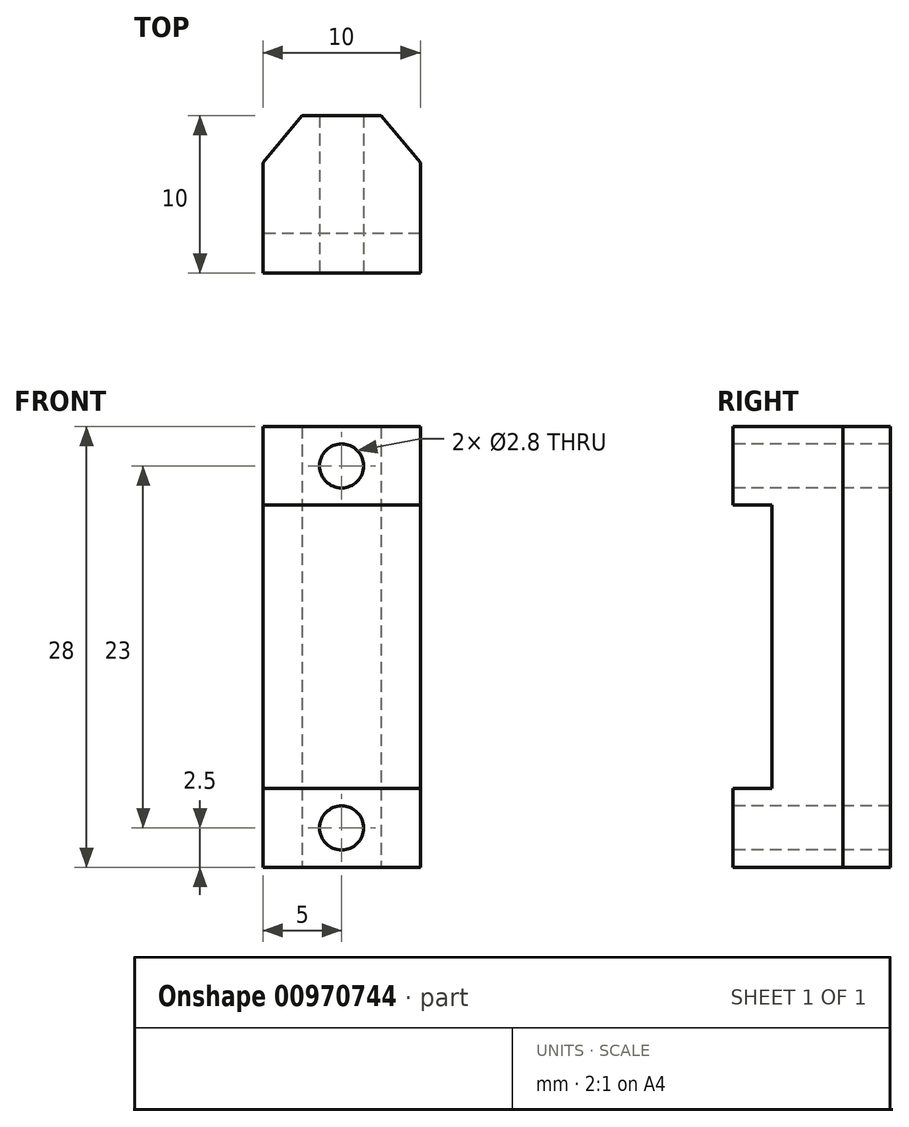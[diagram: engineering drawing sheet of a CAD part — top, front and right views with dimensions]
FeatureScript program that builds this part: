
annotation { "Feature Type Name" : "Feature", "Feature Type Description" : "" }
export const myFeature = defineFeature(function(context is Context, id is Id, definition is map)
    precondition{}
    {
        {
            var Q0;
            Q0=qCreatedBy(makeId("Top.planeOp"),FACE);
            var sketch = newSketch(context, id + "F0", { "sketchPlane" : qUnion([Q0])});
            skLineSegment(sketch, "E0.bottom", {"start": v(0, 0) * mm, "end": v(10, 0) * mm});
            skLineSegment(sketch, "E0.top", {"start": v(2.5, 10) * mm, "end": v(7.5, 10) * mm});
            skLineSegment(sketch, "E0.left", {"start": v(0, 0) * mm, "end": v(0, 7) * mm});
            skLineSegment(sketch, "E0.right", {"start": v(10, 0) * mm, "end": v(10, 7) * mm});
            skLineSegment(sketch, "E1", {"start": v(7.5, 10) * mm, "end": v(10, 7) * mm});
            skLineSegment(sketch, "E2", {"start": v(0, 7) * mm, "end": v(2.5, 10) * mm});
            skSolve(sketch);
        }
        {
            var Q0;
            Q0=makeQuery(id+"F0.imprint","IMPRINT",FACE,{"disambiguationData":[TD([[makeQuery(id+"F0.imprint","IMPRINT",EDGE,{"derivedFrom":sQuery(id+"F0.wireOp",EDGE,"E0.bottom")}),1.0]])]});
            extrude(context, id + "F1", {"entities" : qUnion([Q0]), "depth" : 28 * mm, "offsetDistance" : 25 * mm});
        }
        {
            var Q0;
            Q0=makeQuery(id+"F1.opExtrude","SWEPT_FACE",FACE,{"disambiguationData":[OSD([sQuery(id+"F0.wireOp",EDGE,"E0.bottom")])]});
            var sketch = newSketch(context, id + "F2", { "sketchPlane" : qUnion([Q0])});
            skLineSegment(sketch, "E3", {"start": v(10, 5) * mm, "end": v(0, 5) * mm});
            skLineSegment(sketch, "E4", {"start": v(10, 23) * mm, "end": v(0, 23) * mm});
            skLineSegment(sketch, "E5", {"start": v(10, 0) * mm, "end": v(0, 5) * mm, "construction": true});
            skLineSegment(sketch, "E6", {"start": v(0, 23) * mm, "end": v(10, 28) * mm, "construction": true});
            skCircle(sketch, "E7", {"center": v(5, 2.5) * mm, "radius": 1.4 * mm});
            skCircle(sketch, "E8", {"center": v(5, 25.5) * mm, "radius": 1.4 * mm});
            skSolve(sketch);
        }
        {
            var Q0;
            {var subQ0=sQuery(id+"F2.wireOp",EDGE,"E3");Q0=makeQuery(id+"F2.imprint","IMPRINT",FACE,{"disambiguationData":[TD([[makeQuery(id+"F2.imprint","IMPRINT",EDGE,{"derivedFrom":subQ0}),-1.0]])]});}
            extrude(context, id + "F3", {"entities" : qUnion([Q0]), "operationType" : NewBodyOperationType.REMOVE, "oppositeDirection" : true, "depth" : 2.5 * mm, "offsetDistance" : 25 * mm});
        }
        {
            var Q0;
            Q0=makeQuery(id+"F2.imprint","IMPRINT",FACE,{"disambiguationData":[TD([[makeQuery(id+"F2.imprint","IMPRINT",EDGE,{"derivedFrom":sQuery(id+"F2.wireOp",EDGE,"E8")}),1.0]])]});
            var Q1;
            Q1=makeQuery(id+"F2.imprint","IMPRINT",FACE,{"disambiguationData":[TD([[makeQuery(id+"F2.imprint","IMPRINT",EDGE,{"derivedFrom":sQuery(id+"F2.wireOp",EDGE,"E7")}),1.0]])]});
            extrude(context, id + "F4", {"entities" : qUnion([Q0, Q1]), "operationType" : NewBodyOperationType.REMOVE, "oppositeDirection" : true, "depth" : 25 * mm, "offsetDistance" : 25 * mm});
        }
    });
